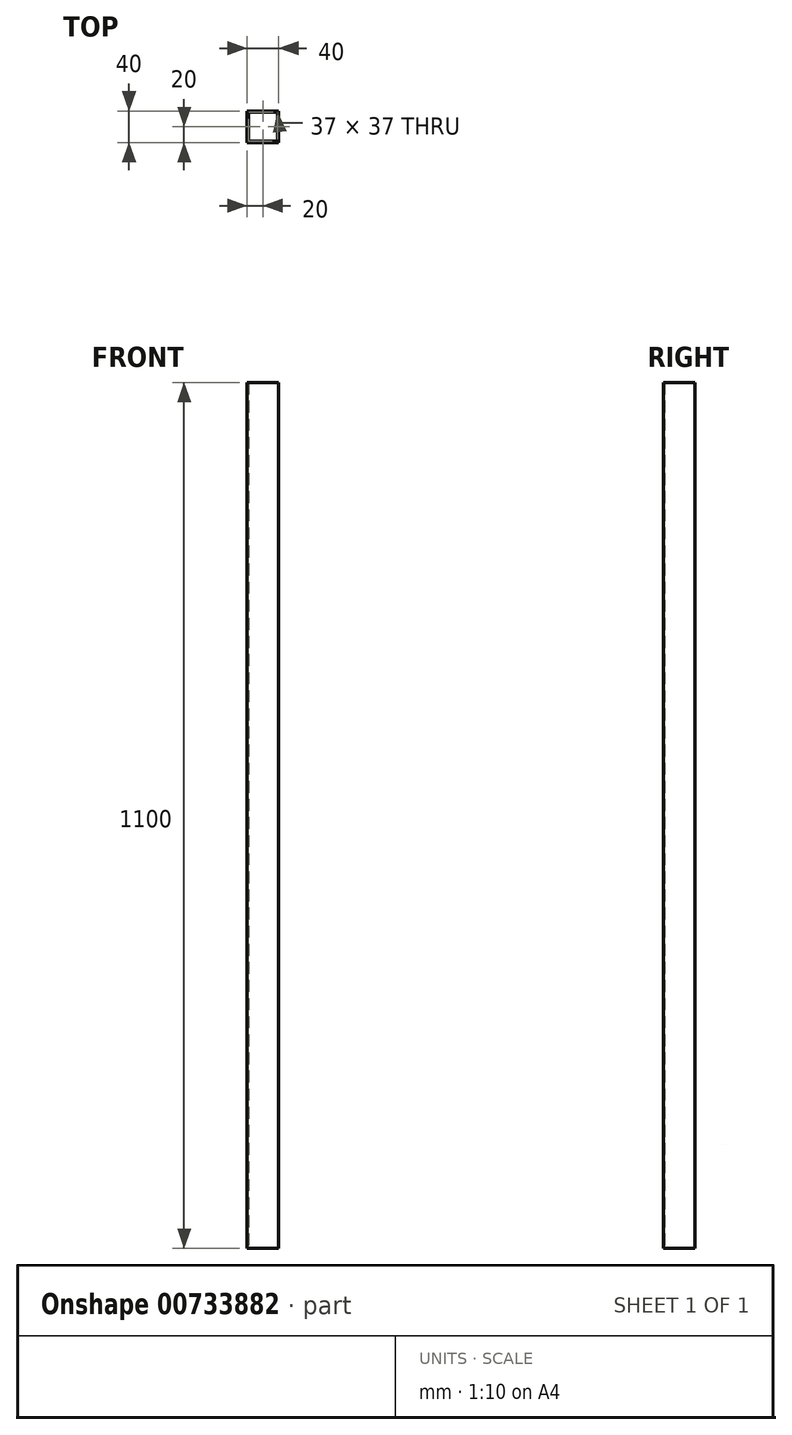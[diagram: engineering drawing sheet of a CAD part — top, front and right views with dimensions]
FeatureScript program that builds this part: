
annotation { "Feature Type Name" : "Feature", "Feature Type Description" : "" }
export const myFeature = defineFeature(function(context is Context, id is Id, definition is map)
    precondition{}
    {
        {
            var Q0;
            Q0=qCreatedBy(makeId("Top.planeOp"),FACE);
            var sketch = newSketch(context, id + "F0", { "sketchPlane" : qUnion([Q0])});
            skLineSegment(sketch, "E0.bottom", {"start": v(20, 20) * mm, "end": v(-20, 20) * mm});
            skLineSegment(sketch, "E0.top", {"start": v(20, -20) * mm, "end": v(-20, -20) * mm});
            skLineSegment(sketch, "E0.left", {"start": v(20, 20) * mm, "end": v(20, -20) * mm});
            skLineSegment(sketch, "E0.right", {"start": v(-20, 20) * mm, "end": v(-20, -20) * mm});
            skPoint(sketch, "E0.middle", {"position": v(0, 0) * mm});
            skLineSegment(sketch, "E1.bottom", {"start": v(18.5, 18.5) * mm, "end": v(-18.5, 18.5) * mm});
            skLineSegment(sketch, "E1.top", {"start": v(18.5, -18.5) * mm, "end": v(-18.5, -18.5) * mm});
            skLineSegment(sketch, "E1.left", {"start": v(18.5, 18.5) * mm, "end": v(18.5, -18.5) * mm});
            skLineSegment(sketch, "E1.right", {"start": v(-18.5, 18.5) * mm, "end": v(-18.5, -18.5) * mm});
            skSolve(sketch);
        }
        {
            var Q0;
            Q0=makeQuery(id+"F0.imprint","IMPRINT",FACE,{"disambiguationData":[TD([[makeQuery(id+"F0.imprint","IMPRINT",EDGE,{"derivedFrom":sQuery(id+"F0.wireOp",EDGE,"E0.bottom")}),1.0]])]});
            extrude(context, id + "F1", {"entities" : qUnion([Q0]), "depth" : 1100 * mm, "offsetDistance" : 25 * mm});
        }
    });
